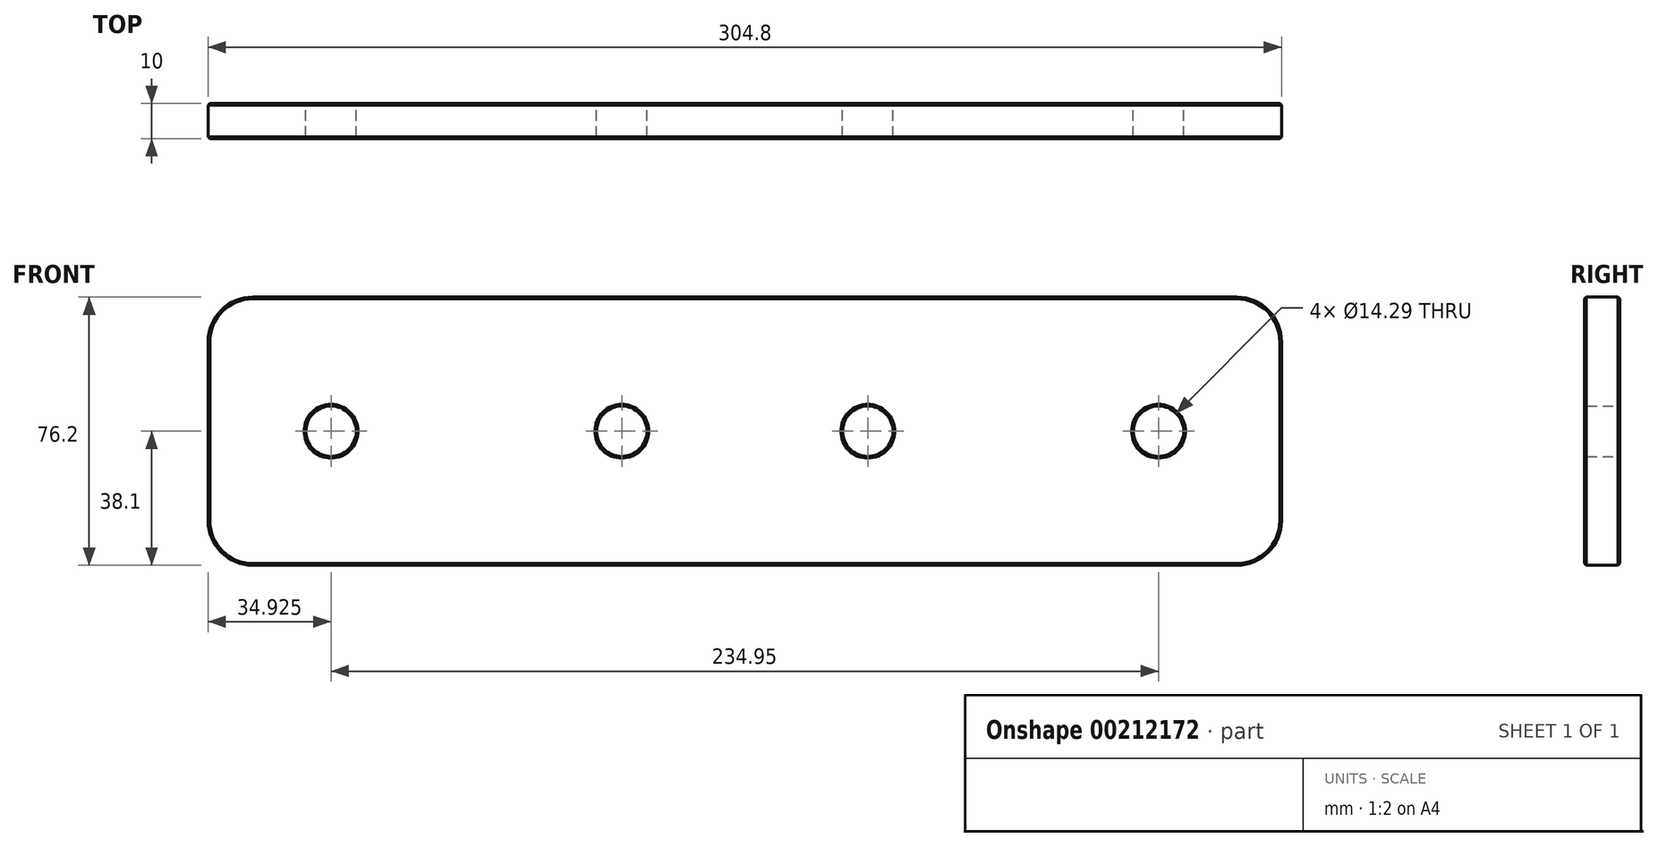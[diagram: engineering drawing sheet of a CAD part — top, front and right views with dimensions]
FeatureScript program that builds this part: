
annotation { "Feature Type Name" : "Feature", "Feature Type Description" : "" }
export const myFeature = defineFeature(function(context is Context, id is Id, definition is map)
    precondition{}
    {
        {
            var Q0;
            Q0=qCreatedBy(makeId("Front.planeOp"),FACE);
            var sketch = newSketch(context, id + "F0", { "sketchPlane" : qUnion([Q0])});
            skLineSegment(sketch, "E0", {"start": v(0, 0) * mm, "end": v(-34.93, 0) * mm, "construction": true});
            skLineSegment(sketch, "E1", {"start": v(-34.93, 0) * mm, "end": v(-117.48, 0) * mm, "construction": true});
            skLineSegment(sketch, "E2", {"start": v(-117.48, 0) * mm, "end": v(-152.4, 0) * mm, "construction": true});
            skLineSegment(sketch, "E3", {"start": v(0, 0) * mm, "end": v(0, 38.1) * mm, "construction": true});
            skLineSegment(sketch, "E4", {"start": v(0, 0) * mm, "end": v(0, -38.1) * mm, "construction": true});
            skCircle(sketch, "E5", {"center": v(-34.93, 0) * mm, "radius": 7.14 * mm});
            skCircle(sketch, "E6", {"center": v(-117.48, 0) * mm, "radius": 7.14 * mm});
            skLineSegment(sketch, "E7", {"start": v(-152.4, 0) * mm, "end": v(-152.4, 25.4) * mm});
            skLineSegment(sketch, "E8", {"start": v(-139.7, 38.1) * mm, "end": v(0, 38.1) * mm});
            skPoint(sketch, "E9.visualSharp", {"position": v(-152.4, 38.1) * mm});
            skArc(sketch, "E9.filletArc", {"start": v(-139.7, 38.1) * mm, "mid": v(-148.68, 34.38) * mm, "end": v(-152.4, 25.4) * mm});
            skLineSegment(sketch, "E10.MirrorCS", {"start": v(-139.7, -38.1) * mm, "end": v(0, -38.1) * mm});
            skArc(sketch, "E11.MirrorCS", {"start": v(-139.7, -38.1) * mm, "mid": v(-148.68, -34.38) * mm, "end": v(-152.4, -25.4) * mm});
            skLineSegment(sketch, "E12.MirrorCS", {"start": v(-152.4, 0) * mm, "end": v(-152.4, -25.4) * mm});
            skLineSegment(sketch, "E13.MirrorCS", {"start": v(139.7, 38.1) * mm, "end": v(0, 38.1) * mm});
            skArc(sketch, "E14.MirrorCS", {"start": v(139.7, 38.1) * mm, "mid": v(148.68, 34.38) * mm, "end": v(152.4, 25.4) * mm});
            skLineSegment(sketch, "E15.MirrorCS", {"start": v(152.4, 0) * mm, "end": v(152.4, 25.4) * mm});
            skLineSegment(sketch, "E16.MirrorCS", {"start": v(152.4, 0) * mm, "end": v(152.4, -25.4) * mm});
            skArc(sketch, "E17.MirrorCS", {"start": v(139.7, -38.1) * mm, "mid": v(148.68, -34.38) * mm, "end": v(152.4, -25.4) * mm});
            skLineSegment(sketch, "E18.MirrorCS", {"start": v(139.7, -38.1) * mm, "end": v(0, -38.1) * mm});
            skCircle(sketch, "E19.MirrorC", {"center": v(34.93, 0) * mm, "radius": 7.14 * mm});
            skCircle(sketch, "E20.MirrorC", {"center": v(117.48, 0) * mm, "radius": 7.14 * mm});
            skSolve(sketch);
        }
        {
            var Q0;
            Q0=makeQuery(id+"F0.imprint","IMPRINT",FACE,{"disambiguationData":[TD([[makeQuery(id+"F0.imprint","IMPRINT",EDGE,{"derivedFrom":sQuery(id+"F0.wireOp",EDGE,"E5")}),-1.0]])]});
            extrude(context, id + "F1", {"entities" : qUnion([Q0]), "depth" : 10 * mm});
        }
        {
            var Q0;
            Q0=makeQuery(id+"F1.opExtrude","CAP_FACE",FACE,{"disambiguationData":[OSD([sQuery(id+"F0.wireOp",EDGE,"E5"),sQuery(id+"F0.wireOp",EDGE,"E6"),sQuery(id+"F0.wireOp",EDGE,"E7"),sQuery(id+"F0.wireOp",EDGE,"E8"),sQuery(id+"F0.wireOp",EDGE,"E9.filletArc"),sQuery(id+"F0.wireOp",EDGE,"E10.MirrorCS"),sQuery(id+"F0.wireOp",EDGE,"E11.MirrorCS"),sQuery(id+"F0.wireOp",EDGE,"E12.MirrorCS"),sQuery(id+"F0.wireOp",EDGE,"E13.MirrorCS"),sQuery(id+"F0.wireOp",EDGE,"E14.MirrorCS"),sQuery(id+"F0.wireOp",EDGE,"E15.MirrorCS"),sQuery(id+"F0.wireOp",EDGE,"E16.MirrorCS"),sQuery(id+"F0.wireOp",EDGE,"E17.MirrorCS"),sQuery(id+"F0.wireOp",EDGE,"E18.MirrorCS"),sQuery(id+"F0.wireOp",EDGE,"E19.MirrorC"),sQuery(id+"F0.wireOp",EDGE,"E20.MirrorC")])],"isStart":false});
            var Q1;
            Q1=makeQuery(id+"F1.opExtrude","CAP_FACE",FACE,{"disambiguationData":[OSD([sQuery(id+"F0.wireOp",EDGE,"E5"),sQuery(id+"F0.wireOp",EDGE,"E6"),sQuery(id+"F0.wireOp",EDGE,"E7"),sQuery(id+"F0.wireOp",EDGE,"E8"),sQuery(id+"F0.wireOp",EDGE,"E9.filletArc"),sQuery(id+"F0.wireOp",EDGE,"E10.MirrorCS"),sQuery(id+"F0.wireOp",EDGE,"E11.MirrorCS"),sQuery(id+"F0.wireOp",EDGE,"E12.MirrorCS"),sQuery(id+"F0.wireOp",EDGE,"E13.MirrorCS"),sQuery(id+"F0.wireOp",EDGE,"E14.MirrorCS"),sQuery(id+"F0.wireOp",EDGE,"E15.MirrorCS"),sQuery(id+"F0.wireOp",EDGE,"E16.MirrorCS"),sQuery(id+"F0.wireOp",EDGE,"E17.MirrorCS"),sQuery(id+"F0.wireOp",EDGE,"E18.MirrorCS"),sQuery(id+"F0.wireOp",EDGE,"E19.MirrorC"),sQuery(id+"F0.wireOp",EDGE,"E20.MirrorC")])],"isStart":true});
            chamfer(context, id + "F2", {"entities" : qUnion([Q0, Q1]), "width" : 0.5 * mm, "tangentPropagation" : true});
        }
    });
